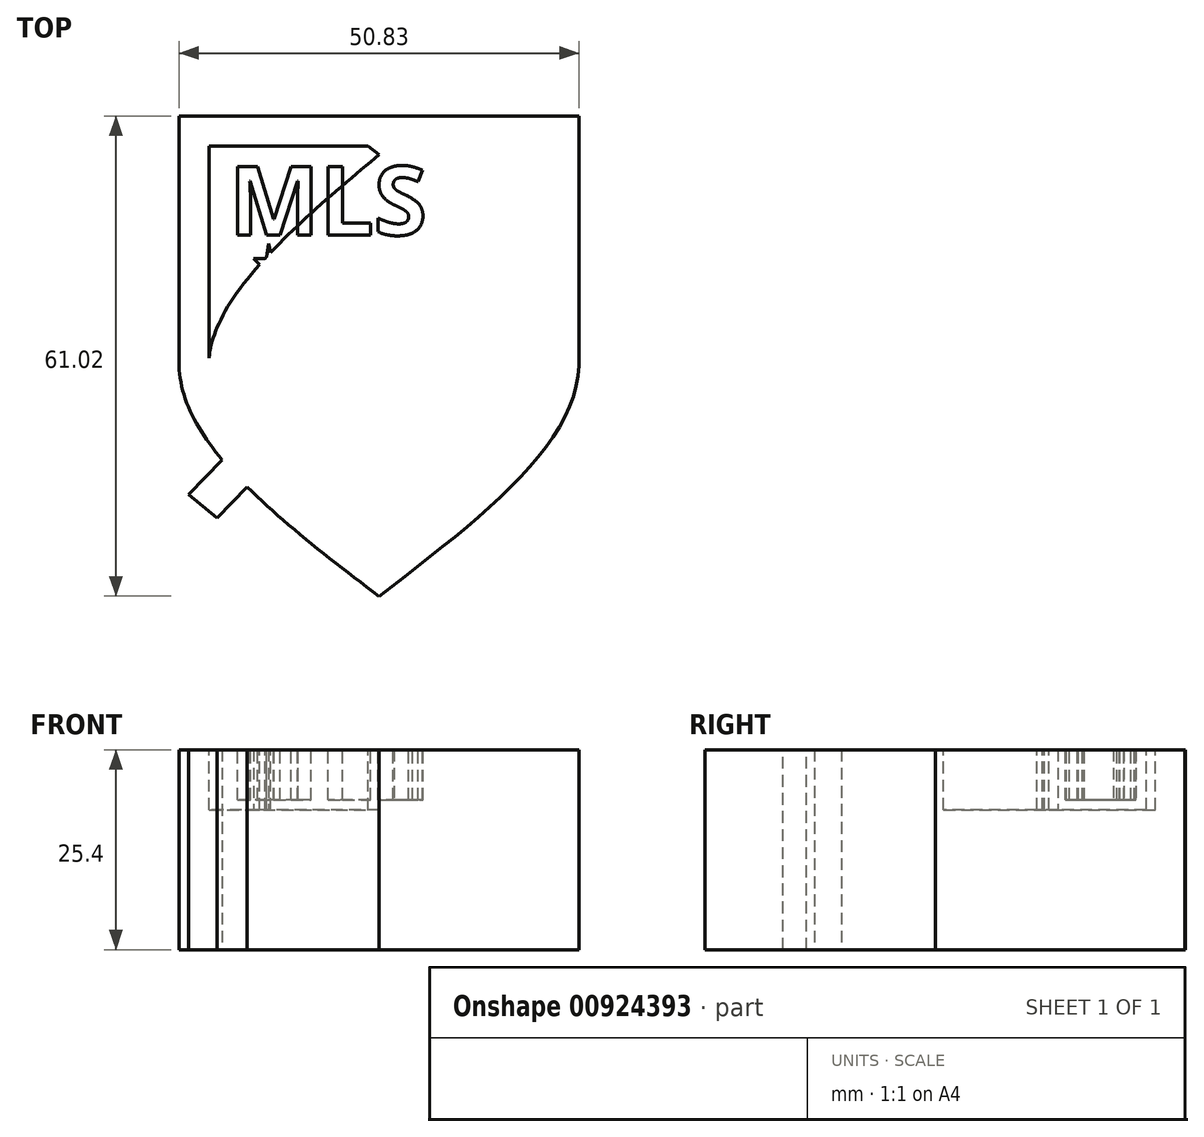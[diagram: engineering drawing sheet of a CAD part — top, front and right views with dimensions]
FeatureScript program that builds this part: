
annotation { "Feature Type Name" : "Feature", "Feature Type Description" : "" }
export const myFeature = defineFeature(function(context is Context, id is Id, definition is map)
    precondition{}
    {
        {
            var Q0;
            Q0=qCreatedBy(makeId("Top.planeOp"),FACE);
            var sketch = newSketch(context, id + "F0", { "sketchPlane" : qUnion([Q0])});
            skLineSegment(sketch, "E0.bottom", {"start": v(0, 0) * mm, "end": v(50.8, 0) * mm});
            skLineSegment(sketch, "E0.top", {"start": v(0, 88.9) * mm, "end": v(50.8, 88.9) * mm});
            skLineSegment(sketch, "E0.left", {"start": v(0, 0) * mm, "end": v(0, 88.9) * mm});
            skLineSegment(sketch, "E0.right", {"start": v(50.8, 0) * mm, "end": v(50.8, 88.9) * mm});
            skSolve(sketch);
        }
        {
            var Q0;
            Q0=makeQuery(id+"F0.imprint","IMPRINT",FACE,{"disambiguationData":[TD([[makeQuery(id+"F0.imprint","IMPRINT",EDGE,{"derivedFrom":sQuery(id+"F0.wireOp",EDGE,"E0.bottom")}),1.0]])]});
            extrude(context, id + "F1", {"entities" : qUnion([Q0]), "depth" : 25.4 * mm, "offsetDistance" : 25.4 * mm});
        }
        {
            var Q0;
            Q0=makeQuery(id+"F1.opExtrude","CAP_FACE",FACE,{"disambiguationData":[OSD([sQuery(id+"F0.wireOp",EDGE,"E0.bottom"),sQuery(id+"F0.wireOp",EDGE,"E0.top"),sQuery(id+"F0.wireOp",EDGE,"E0.left"),sQuery(id+"F0.wireOp",EDGE,"E0.right")])],"isStart":false});
            var sketch = newSketch(context, id + "F2", { "sketchPlane" : qUnion([Q0])});
            skPoint(sketch, "E1", {"position": v(0, 57.15) * mm});
            skSolve(sketch);
        }
        {
            var Q0;
            Q0=makeQuery(id+"F2.imprint","IMPRINT",FACE,{"disambiguationData":[TD([[makeQuery(id+"F2.imprint","IMPRINT",EDGE,{"derivedFrom":makeQuery(id+"F1.opExtrude","CAP_EDGE",EDGE,{"disambiguationData":[OSD([sQuery(id+"F0.wireOp",EDGE,"E0.bottom")])],"isStart":false})}),1.0]])]});
            var sketch = newSketch(context, id + "F3", { "sketchPlane" : qUnion([Q0])});
            skPoint(sketch, "E2", {"position": v(50.8, 57.15) * mm});
            skSolve(sketch);
        }
        {
            var Q0;
            Q0=makeQuery(id+"F3.imprint","IMPRINT",FACE,{"disambiguationData":[TD([[makeQuery(id+"F3.imprint","IMPRINT",EDGE,{"derivedFrom":makeQuery(id+"F2.imprint","IMPRINT",EDGE,{"derivedFrom":makeQuery(id+"F1.opExtrude","CAP_EDGE",EDGE,{"disambiguationData":[OSD([sQuery(id+"F0.wireOp",EDGE,"E0.bottom")])],"isStart":false})})}),1.0]])]});
            var sketch = newSketch(context, id + "F4", { "sketchPlane" : qUnion([Q0])});
            skPoint(sketch, "E3", {"position": v(25.4, 27.94) * mm});
            skLineSegment(sketch, "E4", {"start": v(1.37, 1.36) * mm, "end": v(-1.37, -1.36) * mm});
            skSolve(sketch);
        }
        {
            var Q0;
            Q0=qCreatedBy(makeId("Top.planeOp"),FACE);
            var sketch = newSketch(context, id + "F5", { "sketchPlane" : qUnion([Q0])});
            skFitSpline(sketch, "E5", {"points": [v(25.42, 27.88) * mm, v(50.8, 57.17) * mm, v(25.42, 88.9) * mm], "startDerivative": vector(76.75, 58.56) * mm, "endDerivative": vector(-76.77, 63.78) * mm});
            skLineSegment(sketch, "E6", {"start": v(25.42, 88.9) * mm, "end": v(25.42, 27.88) * mm});
            skPoint(sketch, "E7.orphan", {"position": v(25.42, 0) * mm});
            skLineSegment(sketch, "E8", {"start": v(50.8, 57.17) * mm, "end": v(50.8, 88.9) * mm});
            skLineSegment(sketch, "E9", {"start": v(50.8, 88.9) * mm, "end": v(25.42, 88.9) * mm});
            skLineSegment(sketch, "E10", {"start": v(50.8, 57.17) * mm, "end": v(50.8, 0) * mm});
            skLineSegment(sketch, "E11", {"start": v(50.8, 0) * mm, "end": v(0, 0) * mm});
            skLineSegment(sketch, "E12", {"start": v(0, 0) * mm, "end": v(0, 88.83) * mm});
            skLineSegment(sketch, "E13", {"start": v(0, 88.83) * mm, "end": v(1, 97.89) * mm});
            skLineSegment(sketch, "E14", {"start": v(1, 97.89) * mm, "end": v(25.95, 97.89) * mm});
            skLineSegment(sketch, "E15", {"start": v(25.95, 97.89) * mm, "end": v(25.42, 88.9) * mm});
            skSolve(sketch);
        }
        {
            var Q0;
            {var subQ1=sQuery(id+"F5.wireOp",EDGE,"E6");Q0=makeQuery(id+"F5.imprint","IMPRINT",FACE,{"disambiguationData":[TD([[makeQuery(id+"F5.imprint","IMPRINT",EDGE,{"derivedFrom":subQ1}),-1.0]])]});}
            extrude(context, id + "F6", {"entities" : qUnion([Q0]), "operationType" : NewBodyOperationType.REMOVE, "endBound" : BoundingType.THROUGH_ALL, "depth" : 19.05 * mm, "offsetDistance" : 25.4 * mm});
        }
        {
            var Q0;
            Q0=makeQuery(id+"F1.opExtrude","SWEPT_BODY",BODY,{"disambiguationData":[OSD([sQuery(id+"F0.wireOp",EDGE,"E0.bottom"),sQuery(id+"F0.wireOp",EDGE,"E0.top"),sQuery(id+"F0.wireOp",EDGE,"E0.left"),sQuery(id+"F0.wireOp",EDGE,"E0.right")])]});
            var Q1;
            Q1=makeQuery(id+"F6.boolean.opBoolean","COPY",FACE,{"derivedFrom":makeQuery(id+"F6.opExtrude","SWEPT_FACE",FACE,{"disambiguationData":[OSD([sQuery(id+"F5.wireOp",EDGE,"E6")])]})});
            mirror(context, id + "F7", {"operationType" : NewBodyOperationType.ADD, "entities" : qUnion([Q0]), "mirrorPlane" : qUnion([Q1])});
        }
        {
            var Q0;
            Q0=makeQuery(id+"F4.imprint","IMPRINT",FACE,{"disambiguationData":[TD([[makeQuery(id+"F4.imprint","IMPRINT",EDGE,{"derivedFrom":makeQuery(id+"F3.imprint","IMPRINT",EDGE,{"derivedFrom":makeQuery(id+"F2.imprint","IMPRINT",EDGE,{"derivedFrom":makeQuery(id+"F1.opExtrude","CAP_EDGE",EDGE,{"disambiguationData":[OSD([sQuery(id+"F0.wireOp",EDGE,"E0.bottom")])],"isStart":false})})})}),1.0]])]});
            var sketch = newSketch(context, id + "F8", { "sketchPlane" : qUnion([Q0])});
            skLineSegment(sketch, "E16", {"start": v(-1.96, 0.58) * mm, "end": v(1.85, 0.58) * mm});
            skLineSegment(sketch, "E17", {"start": v(1.85, 0.58) * mm, "end": v(-0.9, -2.23) * mm});
            skLineSegment(sketch, "E18", {"start": v(-0.9, -2.23) * mm, "end": v(-0.06, 2.73) * mm});
            skPoint(sketch, "E18.endSnap0", {"position": v(-0.06, 0.58) * mm});
            skLineSegment(sketch, "E19", {"start": v(-0.06, 2.73) * mm, "end": v(1.13, -2.23) * mm});
            skLineSegment(sketch, "E20", {"start": v(1.13, -2.23) * mm, "end": v(-1.96, 0.58) * mm});
            skSolve(sketch);
        }
        {
            var Q0;
            Q0=makeQuery(id+"F8.imprint","IMPRINT",FACE,{"disambiguationData":[TD([[makeQuery(id+"F8.imprint","IMPRINT",EDGE,{"derivedFrom":makeQuery(id+"F4.imprint","IMPRINT",EDGE,{"derivedFrom":makeQuery(id+"F3.imprint","IMPRINT",EDGE,{"derivedFrom":makeQuery(id+"F2.imprint","IMPRINT",EDGE,{"derivedFrom":makeQuery(id+"F1.opExtrude","CAP_EDGE",EDGE,{"disambiguationData":[OSD([sQuery(id+"F0.wireOp",EDGE,"E0.bottom")])],"isStart":false})})})})}),1.0]])]});
            var sketch = newSketch(context, id + "F9", { "sketchPlane" : qUnion([Q0])});
            skLineSegment(sketch, "E21.0", {"start": v(0.03, 85.1) * mm, "end": v(50.8, 85.1) * mm});
            skLineSegment(sketch, "E22.0", {"start": v(46.99, 57.17) * mm, "end": v(46.99, 88.9) * mm});
            skLineSegment(sketch, "E23.0", {"start": v(3.84, 57.17) * mm, "end": v(3.84, 88.9) * mm});
            skFitSpline(sketch, "E24.0", {"points": [v(27.85, 85.97) * mm, v(26.25, 84.64) * mm, v(23.08, 82) * mm, v(18.53, 78.09) * mm, v(14.35, 74.23) * mm, v(10.67, 70.46) * mm, v(7.65, 66.82) * mm, v(5.8, 63.95) * mm, v(4.78, 61.8) * mm, v(4.24, 60.28) * mm, v(3.92, 58.84) * mm, v(3.82, 57.72) * mm, v(3.85, 56.85) * mm, v(3.95, 55.96) * mm, v(4.2, 54.81) * mm, v(4.72, 53.36) * mm, v(5.71, 51.33) * mm, v(7.53, 48.62) * mm, v(10.53, 45.22) * mm, v(14.2, 41.71) * mm, v(18.4, 38.15) * mm, v(22.95, 34.55) * mm, v(26.13, 32.12) * mm, v(27.73, 30.9) * mm]});
            skFitSpline(sketch, "E25.0", {"points": [v(22.98, 85.97) * mm, v(24.58, 84.64) * mm, v(27.75, 82) * mm, v(32.3, 78.09) * mm, v(36.49, 74.23) * mm, v(40.16, 70.46) * mm, v(43.18, 66.82) * mm, v(45.03, 63.95) * mm, v(46.05, 61.8) * mm, v(46.6, 60.28) * mm, v(46.92, 58.84) * mm, v(47, 57.72) * mm, v(46.98, 56.85) * mm, v(46.88, 55.96) * mm, v(46.63, 54.81) * mm, v(46.12, 53.36) * mm, v(45.12, 51.33) * mm, v(43.3, 48.62) * mm, v(40.3, 45.22) * mm, v(36.63, 41.71) * mm, v(32.44, 38.15) * mm, v(27.88, 34.55) * mm, v(24.7, 32.12) * mm, v(23.1, 30.9) * mm]});
            skSolve(sketch);
        }
        {
            var Q0;
            {var subQ1=sQuery(id+"F9.wireOp",EDGE,"E23.0");var subQ5=sQuery(id+"F9.wireOp",EDGE,"E21.0");var subQ6=makeQuery(id+"F9.imprint","INTERSECT",VERTEX,{"derivedFrom":[subQ5,subQ1]});Q0=makeQuery(id+"F9.imprint","IMPRINT",FACE,{"disambiguationData":[TD([[makeQuery(id+"F9.imprint","IMPRINT",EDGE,{"disambiguationData":[TD([[subQ6,-1.0]])],"derivedFrom":subQ5}),-1.0]])]});}
            extrude(context, id + "F10", {"entities" : qUnion([Q0]), "operationType" : NewBodyOperationType.REMOVE, "oppositeDirection" : true, "depth" : 7.62 * mm, "offsetDistance" : 25.4 * mm});
        }
        {
            var Q0;
            Q0=makeQuery(id+"F8.imprint","IMPRINT",FACE,{"disambiguationData":[TD([[makeQuery(id+"F8.imprint","IMPRINT",EDGE,{"derivedFrom":makeQuery(id+"F4.imprint","IMPRINT",EDGE,{"derivedFrom":makeQuery(id+"F3.imprint","IMPRINT",EDGE,{"derivedFrom":makeQuery(id+"F2.imprint","IMPRINT",EDGE,{"derivedFrom":makeQuery(id+"F1.opExtrude","CAP_EDGE",EDGE,{"disambiguationData":[OSD([sQuery(id+"F0.wireOp",EDGE,"E0.bottom")])],"isStart":false})})})})}),1.0]])]});
            var sketch = newSketch(context, id + "F11", { "sketchPlane" : qUnion([Q0])});
            skLineSegment(sketch, "E26", {"start": v(1.25, 40.77) * mm, "end": v(47.4, 88.63) * mm});
            skLineSegment(sketch, "E27", {"start": v(47.4, 88.63) * mm, "end": v(50.73, 85.41) * mm});
            skLineSegment(sketch, "E28", {"start": v(50.73, 85.41) * mm, "end": v(4.84, 37.82) * mm});
            skLineSegment(sketch, "E29", {"start": v(4.84, 37.82) * mm, "end": v(1.25, 40.77) * mm});
            skSolve(sketch);
        }
        {
            var Q0;
            Q0=makeQuery(id+"F11.imprint","IMPRINT",FACE,{"disambiguationData":[TD([[makeQuery(id+"F11.imprint","IMPRINT",EDGE,{"derivedFrom":sQuery(id+"F11.wireOp",EDGE,"E26")}),-1.0]])]});
            extrude(context, id + "F12", {"entities" : qUnion([Q0]), "operationType" : NewBodyOperationType.ADD, "oppositeDirection" : true, "depth" : 25.4 * mm, "offsetDistance" : 25.4 * mm});
        }
        {
            var Q0;
            Q0=makeQuery(id+"F8.imprint","IMPRINT",FACE,{"disambiguationData":[TD([[makeQuery(id+"F8.imprint","IMPRINT",EDGE,{"derivedFrom":makeQuery(id+"F4.imprint","IMPRINT",EDGE,{"derivedFrom":makeQuery(id+"F3.imprint","IMPRINT",EDGE,{"derivedFrom":makeQuery(id+"F2.imprint","IMPRINT",EDGE,{"derivedFrom":makeQuery(id+"F1.opExtrude","CAP_EDGE",EDGE,{"disambiguationData":[OSD([sQuery(id+"F0.wireOp",EDGE,"E0.bottom")])],"isStart":false})})})})}),1.0]])]});
            var sketch = newSketch(context, id + "F13", { "sketchPlane" : qUnion([Q0])});
            skText(sketch, "E30", { "text": "MLS", "fontName": "OpenSans-Bold.ttf"});
            const initialGuessF13  = {"E30": [0.00638, 0.07377, 1, 0, 0.00878]};
            skSetInitialGuess(sketch, initialGuessF13);
            skSolve(sketch);
        }
        {
            var Q0;
            Q0 = qSketchRegion(id + "F13", true);
            extrude(context, id + "F14", {"entities" : qUnion([Q0]), "oppositeDirection" : true, "depth" : 6.35 * mm, "offsetDistance" : 25.4 * mm});
        }
        {
            var Q0;
            Q0=qCreatedBy(makeId("Top.planeOp"),FACE);
            var sketch = newSketch(context, id + "F15", { "sketchPlane" : qUnion([Q0])});
            skLineSegment(sketch, "E31", {"start": v(9.48, 70.75) * mm, "end": v(13.34, 70.75) * mm});
            skLineSegment(sketch, "E32", {"start": v(13.34, 70.75) * mm, "end": v(10.64, 68) * mm});
            skLineSegment(sketch, "E33", {"start": v(10.64, 68) * mm, "end": v(11.41, 72.68) * mm});
            skLineSegment(sketch, "E34", {"start": v(11.41, 72.68) * mm, "end": v(12.52, 68) * mm});
            skLineSegment(sketch, "E35", {"start": v(12.52, 68) * mm, "end": v(9.48, 70.75) * mm});
            skLineSegment(sketch, "E36", {"start": v(-2, 0.72) * mm, "end": v(1.86, 0.72) * mm});
            skLineSegment(sketch, "E37", {"start": v(1.86, 0.72) * mm, "end": v(-0.84, -2.04) * mm});
            skLineSegment(sketch, "E38", {"start": v(-0.84, -2.04) * mm, "end": v(-0.07, 2.65) * mm});
            skLineSegment(sketch, "E39", {"start": v(-0.07, 2.65) * mm, "end": v(1.04, -2.04) * mm});
            skLineSegment(sketch, "E40", {"start": v(1.04, -2.04) * mm, "end": v(-2, 0.72) * mm});
            skSolve(sketch);
        }
        {
            var Q0;
            Q0=qCreatedBy(makeId("Top.planeOp"),FACE);
            var sketch = newSketch(context, id + "F16", { "sketchPlane" : qUnion([Q0])});
            skLineSegment(sketch, "E41", {"start": v(19.54, 71.1) * mm, "end": v(23.44, 71.1) * mm});
            skLineSegment(sketch, "E42", {"start": v(23.44, 71.1) * mm, "end": v(20.79, 68.3) * mm});
            skLineSegment(sketch, "E43", {"start": v(20.79, 68.3) * mm, "end": v(21.5, 72.35) * mm});
            skLineSegment(sketch, "E44", {"start": v(21.5, 72.35) * mm, "end": v(22.58, 68.3) * mm});
            skLineSegment(sketch, "E45", {"start": v(22.58, 68.3) * mm, "end": v(19.54, 71.1) * mm});
            skSolve(sketch);
        }
        {
            var Q0;
            Q0 = qSketchRegion(id + "F15", true);
            extrude(context, id + "F17", {"entities" : qUnion([Q0]), "operationType" : NewBodyOperationType.ADD, "depth" : 25.4 * mm, "offsetDistance" : 25.4 * mm});
        }
        {
            var Q0;
            Q0 = qSketchRegion(id + "F16", true);
            extrude(context, id + "F18", {"entities" : qUnion([Q0]), "operationType" : NewBodyOperationType.ADD, "depth" : 25.4 * mm, "offsetDistance" : 25.4 * mm});
        }
        {
            var Q0;
            Q0=qCreatedBy(makeId("Top.planeOp"),FACE);
            var sketch = newSketch(context, id + "F19", { "sketchPlane" : qUnion([Q0])});
            skLineSegment(sketch, "E46", {"start": v(14.17, 65.28) * mm, "end": v(18.02, 65.28) * mm});
            skLineSegment(sketch, "E47", {"start": v(18.02, 65.28) * mm, "end": v(15.42, 62.4) * mm});
            skLineSegment(sketch, "E48", {"start": v(15.42, 62.4) * mm, "end": v(16.07, 66.67) * mm});
            skLineSegment(sketch, "E49", {"start": v(16.07, 66.67) * mm, "end": v(17.32, 62.4) * mm});
            skLineSegment(sketch, "E50", {"start": v(17.32, 62.4) * mm, "end": v(14.17, 65.28) * mm});
            skSolve(sketch);
        }
        {
            var Q0;
            Q0 = qSketchRegion(id + "F19", true);
            extrude(context, id + "F20", {"entities" : qUnion([Q0]), "operationType" : NewBodyOperationType.ADD, "depth" : 25.4 * mm, "offsetDistance" : 25.4 * mm});
        }
        {
            var Q0;
            Q0=makeQuery(id+"F17.opExtrude","SWEPT_BODY",BODY,{"disambiguationData":[OSD([sQuery(id+"F15.wireOp",EDGE,"E36"),sQuery(id+"F15.wireOp",EDGE,"E37"),sQuery(id+"F15.wireOp",EDGE,"E38"),sQuery(id+"F15.wireOp",EDGE,"E39"),sQuery(id+"F15.wireOp",EDGE,"E40")])]});
            deleteBodies(context, id + "F21", {"entities" : qUnion([Q0])});
        }
    });
